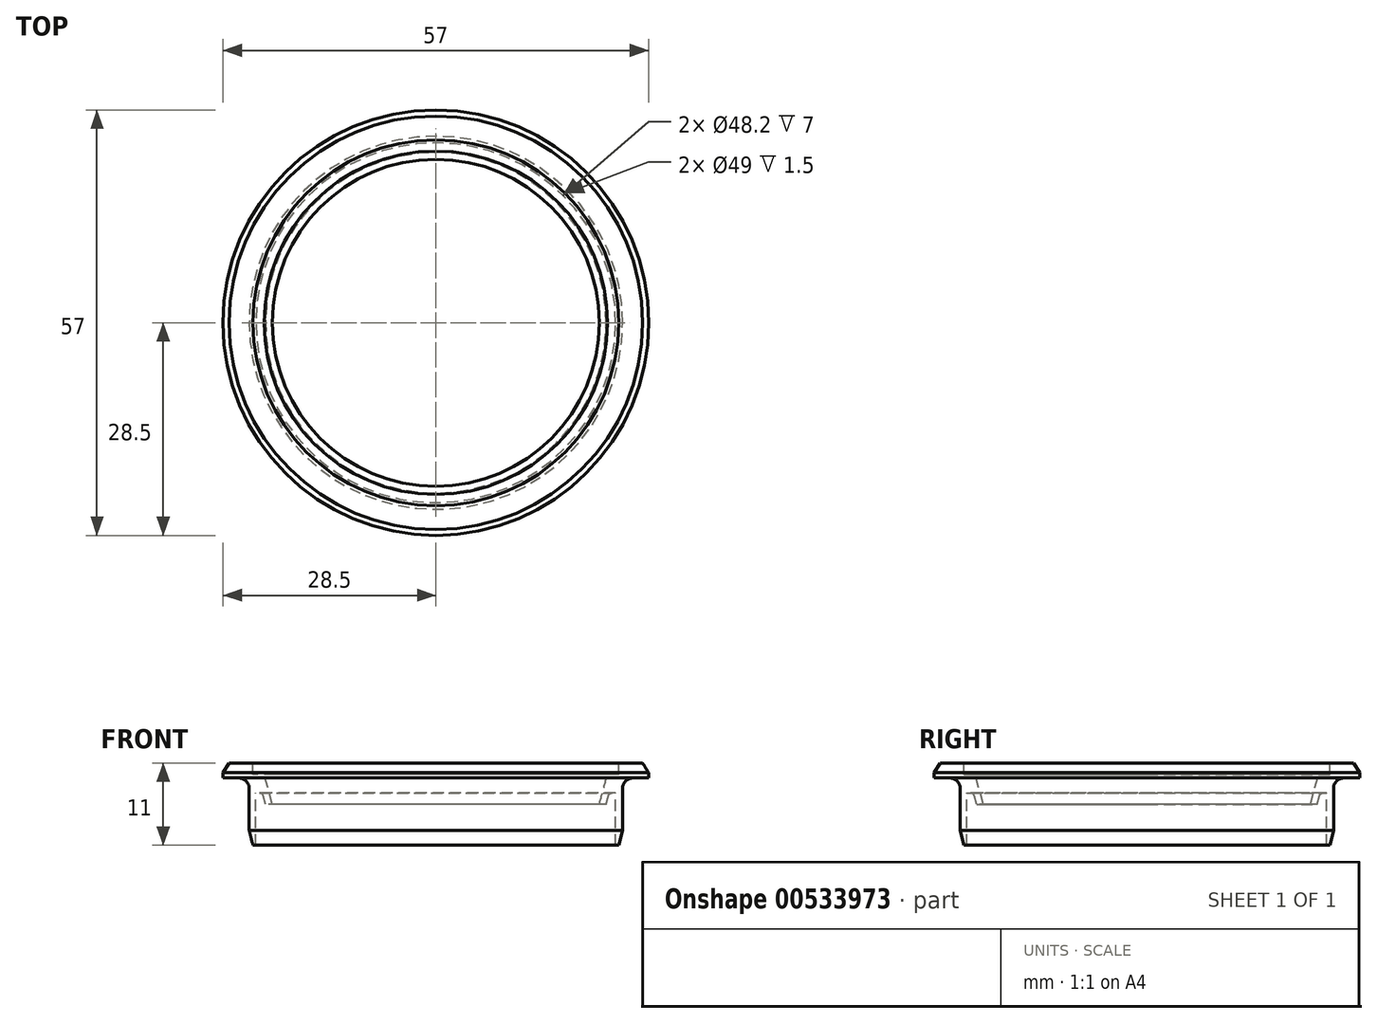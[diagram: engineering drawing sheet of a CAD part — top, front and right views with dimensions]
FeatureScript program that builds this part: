
annotation { "Feature Type Name" : "Feature", "Feature Type Description" : "" }
export const myFeature = defineFeature(function(context is Context, id is Id, definition is map)
    precondition{}
    {
        {
            var Q0;
            Q0=qCreatedBy(makeId("Front.planeOp"),FACE);
            var sketch = newSketch(context, id + "F0", { "sketchPlane" : qUnion([Q0])});
            skLineSegment(sketch, "E0", {"start": v(-28.5, 0) * mm, "end": v(-28.5, -2) * mm});
            skLineSegment(sketch, "E1", {"start": v(-28.5, -2) * mm, "end": v(-25, -2) * mm});
            skLineSegment(sketch, "E2", {"start": v(-25, -2) * mm, "end": v(-25, -11) * mm});
            skLineSegment(sketch, "E3", {"start": v(-25, -11) * mm, "end": v(-24.1, -11) * mm});
            skLineSegment(sketch, "E4", {"start": v(-24.1, -11) * mm, "end": v(-24.1, -4) * mm});
            skLineSegment(sketch, "E5", {"start": v(-24.1, -4) * mm, "end": v(-23.23, -4) * mm});
            skLineSegment(sketch, "E6", {"start": v(-23.23, -4) * mm, "end": v(-22.81, -5.5) * mm});
            skLineSegment(sketch, "E7", {"start": v(-22.81, -5.5) * mm, "end": v(-21.9, -5.5) * mm});
            skLineSegment(sketch, "E8", {"start": v(-21.9, -5.5) * mm, "end": v(-23, -1.5) * mm});
            skLineSegment(sketch, "E9", {"start": v(-23, -1.5) * mm, "end": v(-24.5, -1.5) * mm});
            skLineSegment(sketch, "E10", {"start": v(-24.5, -1.5) * mm, "end": v(-24.5, 0) * mm});
            skLineSegment(sketch, "E11", {"start": v(-24.5, 0) * mm, "end": v(-28.5, 0) * mm});
            skLineSegment(sketch, "E12", {"start": v(0, 17.82) * mm, "end": v(0, -15.68) * mm});
            skSolve(sketch);
        }
        {
            var Q0;
            Q0 = qSketchRegion(id + "F0", true);
            var Q1;
            Q1=sQuery(id+"F0.wireOp",EDGE,"E12");
            revolve(context, id + "F1", {"entities" : qUnion([Q0]), "axis" : qUnion([Q1]), "revolveType" : RevolveType.FULL});
        }
        {
            var Q0;
            Q0=makeQuery(id+"F1.opRevolve","SWEPT_EDGE",EDGE,{"disambiguationData":[OSD([sQuery(id+"F0.wireOp",EDGE,"E0"),sQuery(id+"F0.wireOp",EDGE,"E11")])]});
            chamfer(context, id + "F2", {"entities" : qUnion([Q0]), "chamferType" : ChamferType.TWO_OFFSETS, "width1" : .8 * mm, "oppositeDirection" : false, "width2" : 1.3 * mm, "tangentPropagation" : true});
        }
        {
            var Q0;
            Q0=makeQuery(id+"F1.opRevolve","SWEPT_EDGE",EDGE,{"disambiguationData":[OSD([sQuery(id+"F0.wireOp",EDGE,"E1"),sQuery(id+"F0.wireOp",EDGE,"E2")])]});
            fillet(context, id + "F3", {"entities" : qUnion([Q0]), "radius" : 1.4 * mm, "tangentPropagation" : true, "allowEdgeOverflow" : false});
        }
        {
            var Q0;
            Q0=makeQuery(id+"F1.opRevolve","SWEPT_EDGE",EDGE,{"disambiguationData":[OSD([sQuery(id+"F0.wireOp",EDGE,"E2"),sQuery(id+"F0.wireOp",EDGE,"E3")])]});
            chamfer(context, id + "F4", {"entities" : qUnion([Q0]), "chamferType" : ChamferType.TWO_OFFSETS, "width1" : 2 * mm, "oppositeDirection" : false, "width2" : .5 * mm, "tangentPropagation" : true});
        }
        {
            var Q0;
            Q0=makeQuery(id+"F1.opRevolve","SWEPT_EDGE",EDGE,{"disambiguationData":[OSD([sQuery(id+"F0.wireOp",EDGE,"E5"),sQuery(id+"F0.wireOp",EDGE,"E6")])]});
            fillet(context, id + "F5", {"entities" : qUnion([Q0]), "radius" : .5 * mm, "tangentPropagation" : true, "allowEdgeOverflow" : false});
        }
    });
